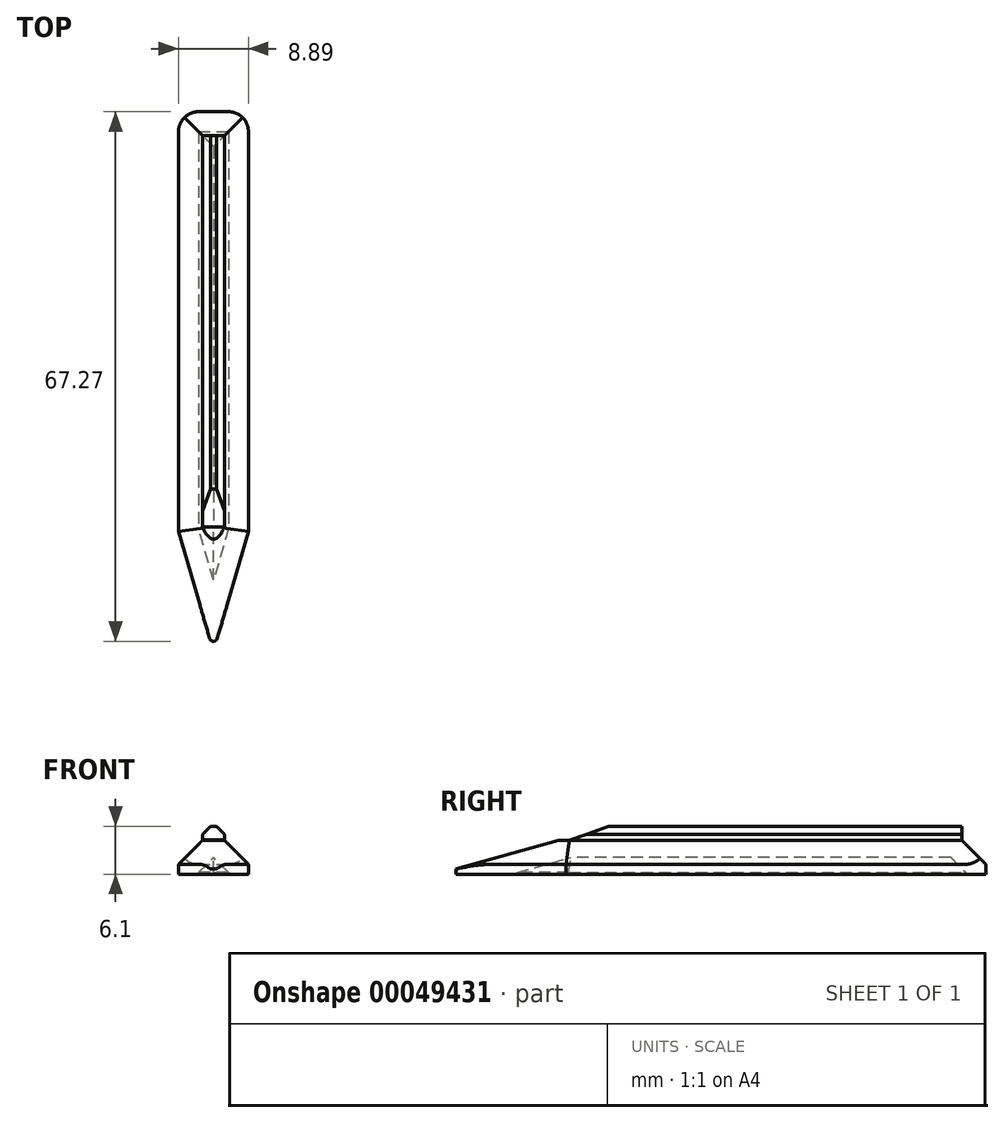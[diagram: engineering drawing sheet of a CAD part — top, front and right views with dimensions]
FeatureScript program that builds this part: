
annotation { "Feature Type Name" : "Feature", "Feature Type Description" : "" }
export const myFeature = defineFeature(function(context is Context, id is Id, definition is map)
    precondition{}
    {
        {
            var Q0;
            Q0=qCreatedBy(makeId("Top.planeOp"),FACE);
            var sketch = newSketch(context, id + "F0", { "sketchPlane" : qUnion([Q0])});
            skLineSegment(sketch, "E0.bottom", {"start": v(0, 0) * mm, "end": v(8.9, 0) * mm});
            skLineSegment(sketch, "E0.top", {"start": v(0, -53.34) * mm, "end": v(8.9, -53.34) * mm});
            skLineSegment(sketch, "E0.left", {"start": v(0, 0) * mm, "end": v(0, -53.34) * mm});
            skLineSegment(sketch, "E0.right", {"start": v(8.9, 0) * mm, "end": v(8.9, -53.34) * mm});
            skLineSegment(sketch, "E1", {"start": v(4.45, -53.34) * mm, "end": v(4.45, -68.58) * mm, "construction": true});
            skLineSegment(sketch, "E2", {"start": v(8.9, -53.34) * mm, "end": v(4.45, -68.58) * mm});
            skLineSegment(sketch, "E3", {"start": v(4.45, -68.58) * mm, "end": v(0, -53.34) * mm});
            skLineSegment(sketch, "E4", {"start": v(4.45, -53.34) * mm, "end": v(4.45, 0) * mm, "construction": true});
            skSolve(sketch);
        }
        {
            var Q0;
            Q0=makeQuery(id+"F0.imprint","IMPRINT",FACE,{"disambiguationData":[TD([[makeQuery(id+"F0.imprint","IMPRINT",EDGE,{"derivedFrom":sQuery(id+"F0.wireOp",EDGE,"E0.bottom")}),-1.0]])]});
            var Q1;
            Q1=makeQuery(id+"F0.imprint","IMPRINT",FACE,{"disambiguationData":[TD([[makeQuery(id+"F0.imprint","IMPRINT",EDGE,{"derivedFrom":sQuery(id+"F0.wireOp",EDGE,"E0.top")}),-1.0]])]});
            extrude(context, id + "F1", {"entities" : qUnion([Q0, Q1]), "depth" : 4.32 * mm});
        }
        {
            var Q0;
            Q0=makeQuery(id+"F1.opExtrude","CAP_EDGE",EDGE,{"disambiguationData":[OSD([sQuery(id+"F0.wireOp",EDGE,"E0.right")])],"isStart":false});
            var Q1;
            Q1=makeQuery(id+"F1.opExtrude","CAP_EDGE",EDGE,{"disambiguationData":[OSD([sQuery(id+"F0.wireOp",EDGE,"E2")])],"isStart":false});
            var Q2;
            Q2=makeQuery(id+"F1.opExtrude","CAP_EDGE",EDGE,{"disambiguationData":[OSD([sQuery(id+"F0.wireOp",EDGE,"E3")])],"isStart":false});
            var Q3;
            Q3=makeQuery(id+"F1.opExtrude","CAP_EDGE",EDGE,{"disambiguationData":[OSD([sQuery(id+"F0.wireOp",EDGE,"E0.left")])],"isStart":false});
            var Q4;
            Q4=makeQuery(id+"F1.opExtrude","CAP_EDGE",EDGE,{"disambiguationData":[OSD([sQuery(id+"F0.wireOp",EDGE,"E0.bottom")])],"isStart":false});
            chamfer(context, id + "F2", {"entities" : qUnion([Q0, Q1, Q2, Q3, Q4]), "width" : 3.05 * mm, "tangentPropagation" : true});
        }
        {
            var Q0;
            Q0=makeQuery(id+"F1.opExtrude","SWEPT_EDGE",EDGE,{"disambiguationData":[OSD([sQuery(id+"F0.wireOp",EDGE,"E2"),sQuery(id+"F0.wireOp",EDGE,"E3")])]});
            fillet(context, id + "F3", {"entities" : qUnion([Q0]), "radius" : 0.5 * mm, "tangentPropagation" : true, "allowEdgeOverflow" : false});
        }
        {
            var Q0;
            Q0=makeQuery(id+"F2.opChamfer","BLEND_EDGE",EDGE,{"blendedFrom":[makeQuery(id+"F1.opExtrude","CAP_EDGE",EDGE,{"disambiguationData":[OSD([sQuery(id+"F0.wireOp",EDGE,"E2")])],"isStart":false}),makeQuery(id+"F1.opExtrude","CAP_EDGE",EDGE,{"disambiguationData":[OSD([sQuery(id+"F0.wireOp",EDGE,"E3")])],"isStart":false})],"blendedInto":[]});
            fillet(context, id + "F4", {"entities" : qUnion([Q0]), "radius" : 2.54 * mm, "tangentPropagation" : true, "allowEdgeOverflow" : false});
        }
        {
            var Q0;
            Q0=makeQuery(id+"F1.opExtrude","SWEPT_EDGE",EDGE,{"disambiguationData":[OSD([sQuery(id+"F0.wireOp",EDGE,"E0.bottom"),sQuery(id+"F0.wireOp",EDGE,"E0.right")])]});
            var Q1;
            Q1=makeQuery(id+"F1.opExtrude","SWEPT_EDGE",EDGE,{"disambiguationData":[OSD([sQuery(id+"F0.wireOp",EDGE,"E0.bottom"),sQuery(id+"F0.wireOp",EDGE,"E0.left")])]});
            fillet(context, id + "F5", {"entities" : qUnion([Q0, Q1]), "radius" : 2.54 * mm, "tangentPropagation" : true, "allowEdgeOverflow" : false});
        }
        {
            var Q0;
            Q0=makeQuery(id+"F1.opExtrude","CAP_FACE",FACE,{"disambiguationData":[OSD([sQuery(id+"F0.wireOp",EDGE,"E0.bottom"),sQuery(id+"F0.wireOp",EDGE,"E0.left"),sQuery(id+"F0.wireOp",EDGE,"E0.right"),sQuery(id+"F0.wireOp",EDGE,"E2"),sQuery(id+"F0.wireOp",EDGE,"E3")])],"isStart":false});
            var sketch = newSketch(context, id + "F6", { "sketchPlane" : qUnion([Q0])});
            skLineSegment(sketch, "E5.bottom", {"start": v(3.05, -3.05) * mm, "end": v(5.84, -3.05) * mm});
            skLineSegment(sketch, "E5.top", {"start": v(3.05, -52.73) * mm, "end": v(5.84, -52.73) * mm});
            skLineSegment(sketch, "E5.left", {"start": v(3.05, -3.05) * mm, "end": v(3.05, -52.73) * mm});
            skLineSegment(sketch, "E5.right", {"start": v(5.84, -3.05) * mm, "end": v(5.84, -52.73) * mm});
            skSolve(sketch);
        }
        {
            var Q0;
            Q0=qSketchRegion(id+"F6",true);
            extrude(context, id + "F7", {"entities" : qUnion([Q0]), "operationType" : NewBodyOperationType.ADD, "depth" : 1.78 * mm});
        }
        {
            var Q0;
            Q0=makeQuery(id+"F7.opExtrude","CAP_EDGE",EDGE,{"disambiguationData":[OSD([sQuery(id+"F6.wireOp",EDGE,"E5.top")])],"isStart":false});
            chamfer(context, id + "F8", {"entities" : qUnion([Q0]), "chamferType" : ChamferType.OFFSET_ANGLE, "width" : 4.83 * mm, "oppositeDirection" : false, "angle" : 20 * degree, "tangentPropagation" : true});
        }
        {
            var Q0;
            Q0=makeQuery(id+"F7.opExtrude","CAP_EDGE",EDGE,{"disambiguationData":[OSD([sQuery(id+"F6.wireOp",EDGE,"E5.right")])],"isStart":false});
            var Q1;
            Q1=makeQuery(id+"F7.opExtrude","CAP_EDGE",EDGE,{"disambiguationData":[OSD([sQuery(id+"F6.wireOp",EDGE,"E5.left")])],"isStart":false});
            chamfer(context, id + "F9", {"entities" : qUnion([Q0, Q1]), "width" : 1.02 * mm, "tangentPropagation" : true});
        }
        {
            var Q0;
            Q0=makeQuery(id+"F1.opExtrude","CAP_FACE",FACE,{"disambiguationData":[OSD([sQuery(id+"F0.wireOp",EDGE,"E0.bottom"),sQuery(id+"F0.wireOp",EDGE,"E0.left"),sQuery(id+"F0.wireOp",EDGE,"E0.right"),sQuery(id+"F0.wireOp",EDGE,"E2"),sQuery(id+"F0.wireOp",EDGE,"E3")])],"isStart":true});
            shell(context, id + "F10", {"entities" : qUnion([Q0]), "thickness" : 2.54 * mm});
        }
    });
